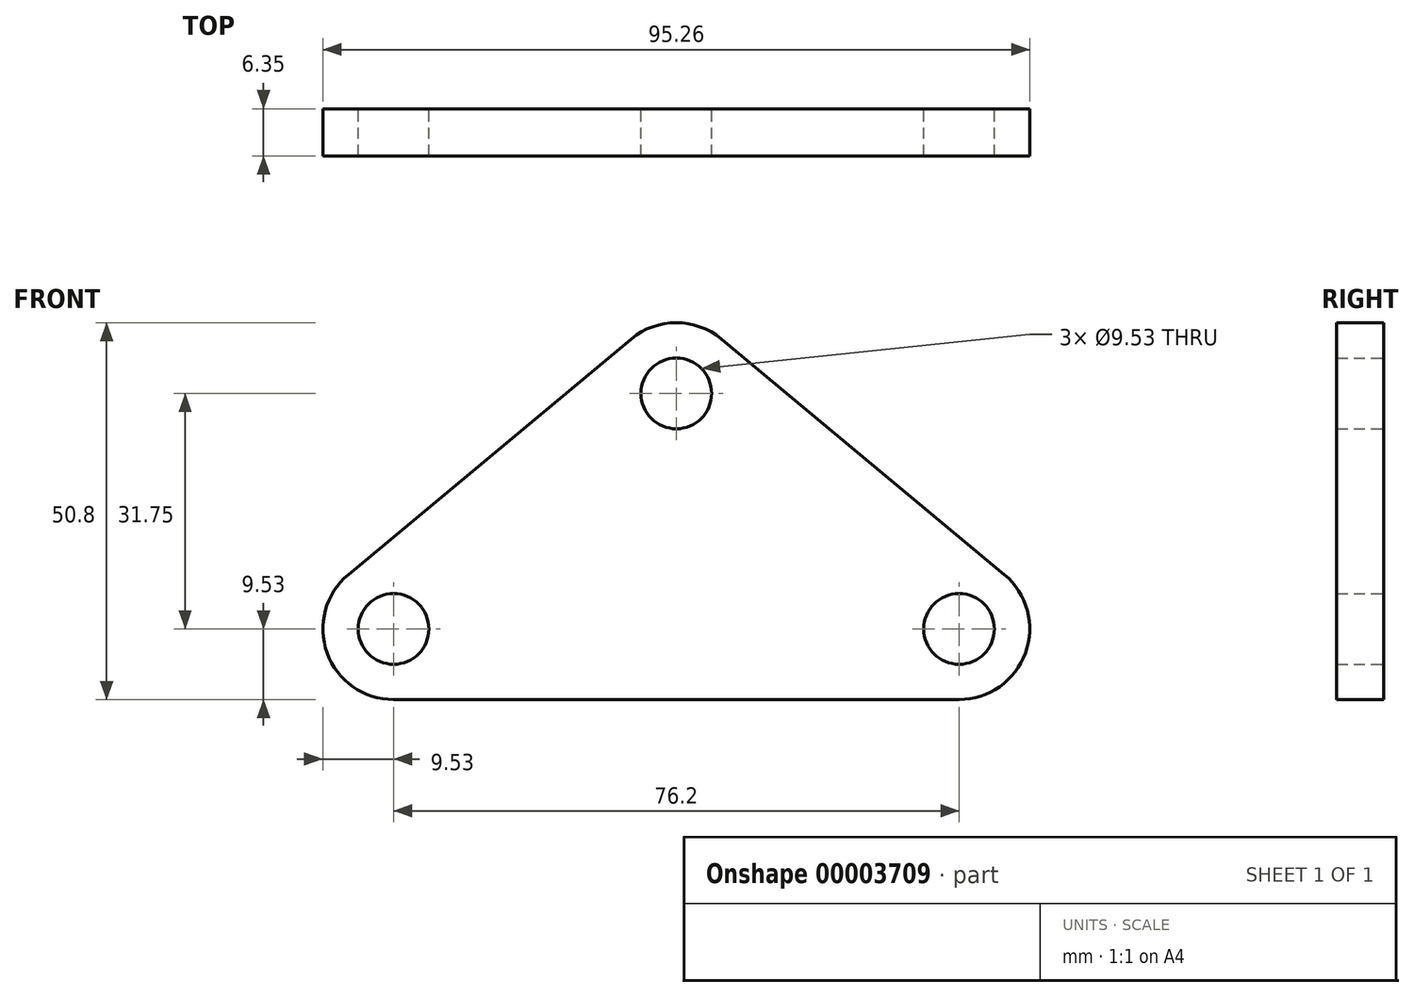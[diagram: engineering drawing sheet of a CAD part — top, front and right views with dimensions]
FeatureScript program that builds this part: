
annotation { "Feature Type Name" : "Feature", "Feature Type Description" : "" }
export const myFeature = defineFeature(function(context is Context, id is Id, definition is map)
    precondition{}
    {
        {
            var Q0;
            Q0=qCreatedBy(makeId("Front.planeOp"),FACE);
            var sketch = newSketch(context, id + "F0", { "sketchPlane" : qUnion([Q0])});
            skCircle(sketch, "E0", {"center": v(0, 0) * mm, "radius": 4.76 * mm});
            skCircle(sketch, "E1", {"center": v(38.1, 31.75) * mm, "radius": 4.76 * mm});
            skCircle(sketch, "E2", {"center": v(76.2, 0) * mm, "radius": 4.76 * mm});
            skArc(sketch, "E3", {"start": v(-6.1, 7.32) * mm, "mid": v(-8.96, -3.24) * mm, "end": v(0, -9.53) * mm});
            skArc(sketch, "E4", {"start": v(76.2, -9.52) * mm, "mid": v(85.16, -3.24) * mm, "end": v(82.3, 7.32) * mm});
            skArc(sketch, "E5", {"start": v(44.2, 39.07) * mm, "mid": v(38.1, 41.28) * mm, "end": v(32, 39.07) * mm});
            skLineSegment(sketch, "E6", {"start": v(-6.1, 7.32) * mm, "end": v(32, 39.07) * mm});
            skLineSegment(sketch, "E7", {"start": v(0, -9.53) * mm, "end": v(76.2, -9.52) * mm});
            skLineSegment(sketch, "E8", {"start": v(82.3, 7.32) * mm, "end": v(44.2, 39.07) * mm});
            skSolve(sketch);
        }
        {
            var Q0;
            Q0 = qSketchRegion(id + "F0", true);
            extrude(context, id + "F1", {"entities" : qUnion([Q0]), "depth" : 6.35 * mm});
        }
    });
